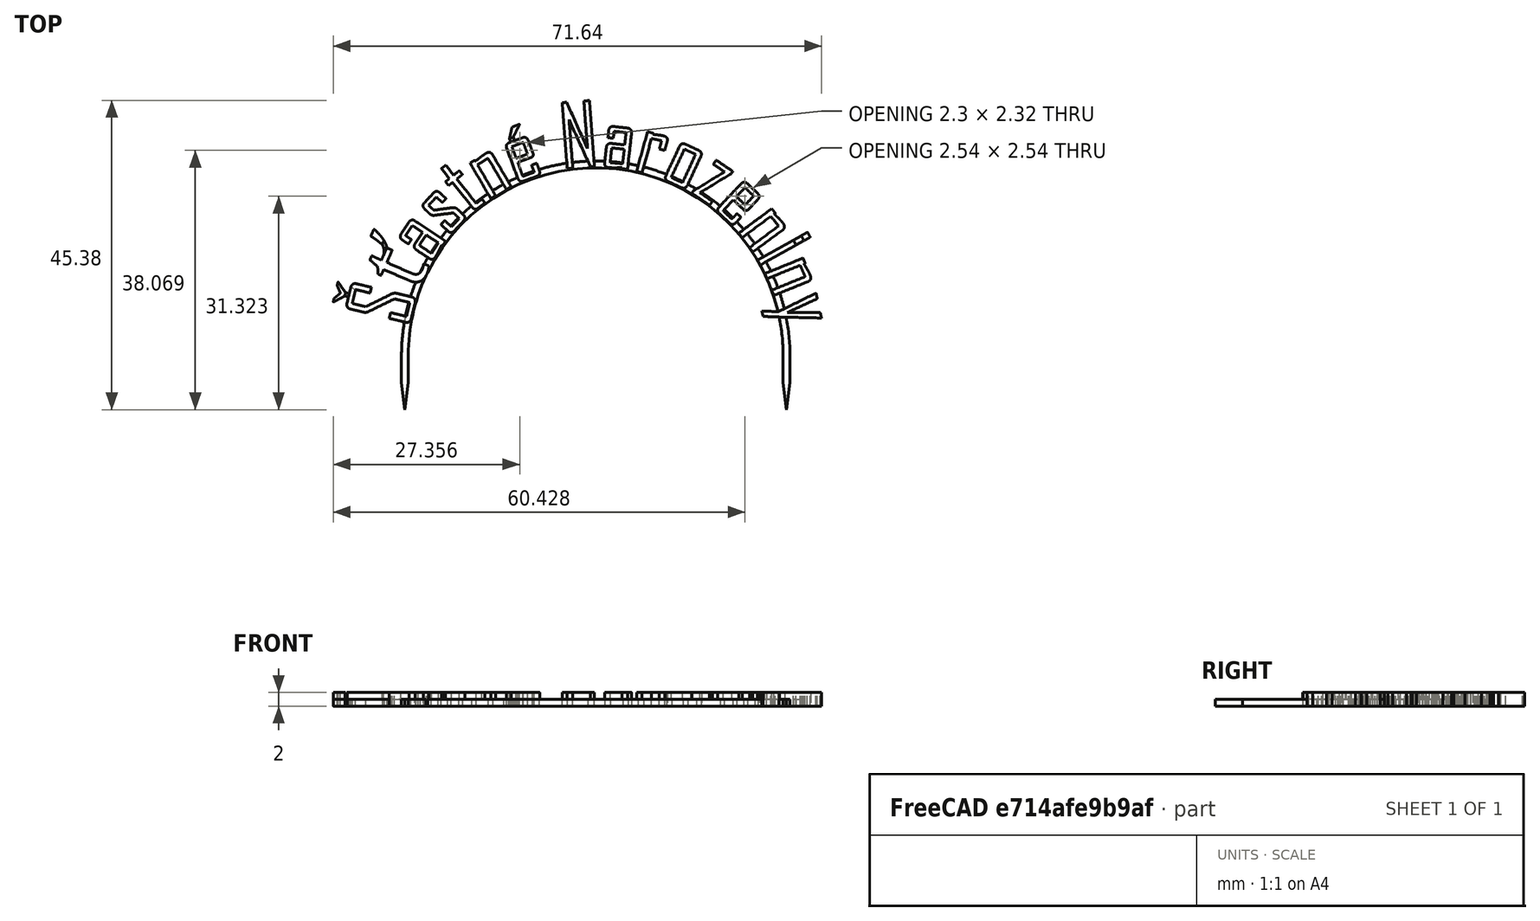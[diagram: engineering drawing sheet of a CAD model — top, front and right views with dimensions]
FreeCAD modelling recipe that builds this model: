
FCSTD DOCUMENT  (FreeCAD 0.20R29177 (Git))
Label: cake-topper-stastne-narozeniny
License: All rights reserved
LicenseURL: http://en.wikipedia.org/wiki/All_rights_reserved
objects: Part::Feature×31, Sketcher::SketchObject×11, PartDesign::Pad×10, App::DocumentObjectGroup×5, PartDesign::Body×2, App::TextDocument×1, Spreadsheet::Sheet×1, PartDesign::Plane×1, App::Part×1, Mesh::Feature×1
note: 65 computed .brp shape members not serialized (recipe doc carries the construction recipe); baked Part::Feature solids carry a one-line shape summary decoded from their .brp

FEATURE [App::TextDocument] Text_document  label="Text document"
FEATURE [Spreadsheet::Sheet] Spreadsheet
  cells = A1=Text height; B1=text_h; C1(dim_text_h)==2mm; A2=Text offset x; B2=text_x; C2(dim_text_x)==-105.3mm; A3=Text offset y; B3=text_y; C3(dim_text_y)==177.4mm; A4=Scaffold height; B4=scaffold_h; C4(dim_scaffold_h)==1mm; A5=Scaffold width; B5=scaffold_w; C5(dim_scaffold_w)==1mm; A6=Scaffold inner radius; B6=scaffold_ir; C6(dim_scaffold_ir)==27.5mm; A7=Scaffold outer radius; B7=scaffold_or; C7(dim_scaffold_or)==dim_scaffold_ir + dim_scaffold_w; A8=Tines length; B8=tine_l; C8(dim_tine_l)==4mm; A9=Tines shaft length; B9=tine_shaft_l; C9(dim_tine_shaft_l)==4mm
FEATURE [PartDesign::Plane] DatumPlane  label="BaseXYDatumPlane"
  Length = 72.6252
  MapMode = 5
  ResizeMode = 0
  Support = -> [XY_Plane]
  Width = 61.0934
FEATURE [Sketcher::SketchObject] Sketch001  label="ArcSketch"
  FullyConstrained = false
  MapMode = 5
  Support = -> [DatumPlane]
  expr: Constraints[15] = Spreadsheet.dim_scaffold_or
  expr: Constraints[37] = Spreadsheet.dim_tine_shaft_l
  expr: Constraints[38] = Spreadsheet.dim_tine_l
  expr: Constraints[59] = Spreadsheet.dim_scaffold_or
  expr: Constraints[6] = Spreadsheet.dim_scaffold_ir
  sketch-geometry (43):
    g0: ArcOfCircle CenterX=0 CenterY=0 CenterZ=0 NormalX=0 NormalY=0 NormalZ=1 AngleXU=0 Radius=27.5 StartAngle=0 EndAngle=3.14159
    g1: LineSegment StartX=-28.5 StartY=3.5e-15 StartZ=0 EndX=-27.5 EndY=3.4e-15 EndZ=0
    g2: LineSegment StartX=27.5 StartY=0 StartZ=0 EndX=28.5 EndY=0 EndZ=0
    g3: ArcOfCircle CenterX=0 CenterY=0 CenterZ=0 NormalX=0 NormalY=0 NormalZ=1 AngleXU=0 Radius=28.5 StartAngle=0 EndAngle=0.501542
    g4: ArcOfCircle CenterX=0 CenterY=0 CenterZ=0 NormalX=0 NormalY=0 NormalZ=1 AngleXU=0 Radius=28.5 StartAngle=0.501542 EndAngle=0.528912
    g5: LineSegment StartX=24.6057 StartY=14.3809 StartZ=0 EndX=31.0393 EndY=18.018 EndZ=0
    g6: LineSegment StartX=24.99 StartY=13.7022 StartZ=0 EndX=31.4232 EndY=17.339 EndZ=0
    g7: LineSegment StartX=31.0393 StartY=18.018 StartZ=0 EndX=31.4232 EndY=17.339 EndZ=0
    g8: LineSegment StartX=-28.5 StartY=3.5e-15 StartZ=0 EndX=-28.5 EndY=-4 EndZ=0
    g9: LineSegment StartX=-27.5 StartY=3.4e-15 StartZ=0 EndX=-27.5 EndY=-4 EndZ=0
    g10: LineSegment StartX=-28.5 StartY=-4 StartZ=0 EndX=-28 EndY=-8 EndZ=0
    g11: LineSegment StartX=-27.5 StartY=-4 StartZ=0 EndX=-28 EndY=-8 EndZ=0
    g12: LineSegment StartX=-28.5 StartY=-4 StartZ=0 EndX=-28 EndY=-4 EndZ=0
    g13: LineSegment StartX=-28 StartY=-4 StartZ=0 EndX=-27.5 EndY=-4 EndZ=0
    g14: LineSegment StartX=-28 StartY=-4 StartZ=0 EndX=-28 EndY=-8 EndZ=0
    g15: LineSegment StartX=27.5 StartY=-4 StartZ=0 EndX=28 EndY=-4 EndZ=0
    g16: LineSegment StartX=28 StartY=-4 StartZ=0 EndX=28.5 EndY=-4 EndZ=0
    g17: LineSegment StartX=28 StartY=-4 StartZ=0 EndX=28 EndY=-8 EndZ=0
    g18: LineSegment StartX=27.5 StartY=0 StartZ=0 EndX=27.5 EndY=-4 EndZ=0
    g19: LineSegment StartX=28.5 StartY=0 StartZ=0 EndX=28.5 EndY=-4 EndZ=0
    g20: LineSegment StartX=27.5 StartY=-4 StartZ=0 EndX=28 EndY=-8 EndZ=0
    g21: LineSegment StartX=28.5 StartY=-4 StartZ=0 EndX=28 EndY=-8 EndZ=0
    g22: LineSegment StartX=28.5 StartY=0 StartZ=0 EndX=28.5 EndY=28.5 EndZ=0
    g23: ArcOfCircle CenterX=0 CenterY=0 CenterZ=0 NormalX=0 NormalY=0 NormalZ=1 AngleXU=0 Radius=28.5 StartAngle=2.25167 EndAngle=2.29659
    g24: LineSegment StartX=-18.9162 StartY=21.3173 StartZ=0 EndX=-27.3759 EndY=31.2933 EndZ=0
    g25: LineSegment StartX=-17.94 StartY=22.1451 StartZ=0 EndX=-26.3997 EndY=32.1211 EndZ=0
    g26: LineSegment StartX=-27.3759 StartY=31.2933 StartZ=0 EndX=-26.3997 EndY=32.1211 EndZ=0
    g27: LineSegment StartX=-17.94 StartY=22.1451 StartZ=0 EndX=0 EndY=22.1451 EndZ=0
    g28: LineSegment StartX=28.5 StartY=28.5 StartZ=0 EndX=0 EndY=28.5 EndZ=0
    g29: LineSegment StartX=0 StartY=28.5 StartZ=0 EndX=-28.5 EndY=28.5 EndZ=0
    g30: LineSegment StartX=-28.5 StartY=3.5e-15 StartZ=0 EndX=-28.5 EndY=28.5 EndZ=0
    g31: ArcOfCircle CenterX=0 CenterY=0 CenterZ=0 NormalX=0 NormalY=0 NormalZ=1 AngleXU=0 Radius=28.5 StartAngle=1.87736 EndAngle=2.25167
    g32: ArcOfCircle CenterX=0 CenterY=0 CenterZ=0 NormalX=0 NormalY=0 NormalZ=1 AngleXU=0 Radius=28.5 StartAngle=0.528912 EndAngle=1.83244
    g33: ArcOfCircle CenterX=0 CenterY=0 CenterZ=0 NormalX=0 NormalY=0 NormalZ=1 AngleXU=0 Radius=28.5 StartAngle=1.83244 EndAngle=1.87736
    g34: LineSegment StartX=-8.60087 StartY=27.1712 StartZ=0 EndX=-12.2687 EndY=39.737 EndZ=0
    g35: LineSegment StartX=-7.37218 StartY=27.53 StartZ=0 EndX=-11.04 EndY=40.0956 EndZ=0
    g36: LineSegment StartX=-12.2687 StartY=39.737 StartZ=0 EndX=-11.04 EndY=40.0956 EndZ=0
    g37: LineSegment StartX=-11.04 StartY=40.0956 StartZ=0 EndX=0 EndY=40.0956 EndZ=0
    g38: LineSegment StartX=-7.37218 StartY=27.53 StartZ=0 EndX=-7.37218 EndY=28.5 EndZ=0
    g39: ArcOfCircle CenterX=0 CenterY=0 CenterZ=0 NormalX=0 NormalY=0 NormalZ=1 AngleXU=0 Radius=28.5 StartAngle=2.71804 EndAngle=3.14159
    g40: ArcOfCircle CenterX=0 CenterY=0 CenterZ=0 NormalX=0 NormalY=0 NormalZ=1 AngleXU=0 Radius=28.5 StartAngle=2.29659 EndAngle=2.67657
    g41: ArcOfCircle CenterX=0 CenterY=0 CenterZ=0 NormalX=0 NormalY=0 NormalZ=1 AngleXU=0 Radius=28.5 StartAngle=2.67657 EndAngle=2.71804
    g42: LineSegment StartX=24.99 StartY=13.7022 StartZ=0 EndX=28.5 EndY=13.7022 EndZ=0
  constraints (115):
    c: Coincident(g0,g-1)
    c: PointOnObject(g0,g-1)
    c: PointOnObject(g0,g-1)
    c: Coincident(g3,g0)
    c: PointOnObject(g39,g-1)
    c: PointOnObject(g3,g-1)
    c: Radius(g0) = 27.5
    c: Coincident(g1,g39)
    c: Coincident(g1,g0)
    c: Coincident(g2,g0)
    c: Coincident(g2,g3)
    c: Coincident(g4,g32)
    c: Coincident(g3,g32)
    c: Coincident(g3,g4)
    c: Coincident(g3,g4)
    c: Radius(g3) = 28.5
    c: Coincident(g5,g32)
    c: Coincident(g6,g3)
    c: Coincident(g7,g5)
    c: Parallel(g5,g6)
    c: Perpendicular(g7,g5)
    c: Coincident(g8,g39)
    c: Vertical(g8)
    c: Coincident(g9,g0)
    c: Vertical(g9)
    c: Coincident(g10,g8)
    c: Coincident(g11,g9)
    c: Coincident(g11,g10)
    c: Coincident(g12,g8)
    c: Horizontal(g12)
    c: Coincident(g13,g12)
    c: Coincident(g13,g9)
    c: Horizontal(g13)
    c: Coincident(g14,g12)
    c: Coincident(g14,g10)
    c: Equal(g13,g12)
    c: Vertical(g14)
    c: DistanceY(g9,g9) = 4
    c: DistanceY(g10,g9) = 4
    c: Horizontal(g15)
    c: Coincident(g16,g15)
    c: Horizontal(g16)
    c: Coincident(g17,g15)
    c: Vertical(g17)
    c: Coincident(g18,g0)
    c: Coincident(g18,g15)
    c: Vertical(g18)
    c: Coincident(g19,g3)
    c: Coincident(g19,g16)
    c: Vertical(g19)
    c: Coincident(g20,g18)
    c: Coincident(g20,g17)
    c: Coincident(g21,g19)
    c: Coincident(g21,g20)
    c: Equal(g18,g9)
    c: Equal(g17,g14)
    c: Equal(g16,g15)
    c: Coincident(g22,g3)
    c: Vertical(g22)
    c: DistanceY(g22,g22) = 28.5
    c: Coincident(g7,g6)
    c: Coincident(g23,g40)
    c: Coincident(g32,g40)
    c: Coincident(g31,g23)
    c: Coincident(g32,g23)
    c: Coincident(g24,g40)
    c: Coincident(g25,g31)
    c: Coincident(g26,g24)
    c: Coincident(g26,g25)
    c: Perpendicular(g24,g26)
    c: Perpendicular(g25,g26)
    c: Coincident(g27,g31)
    c: PointOnObject(g27,g-2)
    c: Horizontal(g27)
    c: Coincident(g28,g22)
    c: PointOnObject(g28,g-2)
    c: Horizontal(g28)
    c: Coincident(g29,g28)
    c: Horizontal(g29)
    c: Coincident(g30,g8)
    c: Coincident(g30,g29)
    c: Vertical(g30)
    c: DistanceX(g27,g27) = 17.94
    c: Distance(g26) = 1.28
    c: Distance(g25) = 13.08
    c: Coincident(g33,g31)
    c: Coincident(g32,g31)
    c: Coincident(g32,g33)
    c: Coincident(g32,g33)
    c: Coincident(g34,g31)
    c: Coincident(g35,g32)
    c: Coincident(g36,g34)
    c: Coincident(g36,g35)
    c: Perpendicular(g34,g36)
    c: Distance(g36) = 1.28
    c: Distance(g31,g32) = 1.28
    c: Distance(g35) = 13.09
    c: Coincident(g37,g35)
    c: PointOnObject(g37,g-2)
    c: Horizontal(g37)
    c: DistanceX(g37,g37) = 11.04
    c: Coincident(g38,g32)
    c: PointOnObject(g38,g29)
    c: Vertical(g38)
    c: DistanceY(g38,g38) = 0.97
    c: Coincident(g41,g39)
    c: Coincident(g40,g39)
    c: Coincident(g40,g41)
    c: Coincident(g40,g41)
    c: Coincident(g42,g3)
    c: PointOnObject(g42,g22)
    c: Horizontal(g42)
    c: Distance(g7) = 0.78
    c: Distance(g6) = 7.39
    c: DistanceX(g42,g42) = 3.51
FEATURE [PartDesign::Pad] Pad  label="ArcPad"
  Direction = (0,0,1)
  Length = 1
  Length2 = 10
  Profile = -> Sketch001
  ReferenceAxis = -> Sketch001 [N_Axis]
  Type = 0
  expr: Length = Spreadsheet.dim_scaffold_h
FEATURE [Part::Feature] path71269
  shape: bbox 10.09 x 5.737 x 2e-07 mm, 0 faces, 0 solids (baked)
FEATURE [Part::Feature] path71269001
  shape: bbox 1.822 x 2.922 x 2e-07 mm, 0 faces, 0 solids (baked)
FEATURE [Part::Feature] path71271
  shape: bbox 8.679 x 5.085 x 2e-07 mm, 0 faces, 0 solids (baked)
FEATURE [Part::Feature] path71271001
  shape: bbox 1.936 x 2.214 x 2e-07 mm, 0 faces, 0 solids (baked)
FEATURE [Part::Feature] path71273
  shape: bbox 6.743 x 5.932 x 2e-07 mm, 0 faces, 0 solids (baked)
FEATURE [Part::Feature] path71273001
  shape: bbox 2.796 x 2.735 x 2e-07 mm, 0 faces, 0 solids (baked)
FEATURE [Part::Feature] path71275
  shape: bbox 6.332 x 6.216 x 2e-07 mm, 0 faces, 0 solids (baked)
FEATURE [Part::Feature] path71277
  shape: bbox 6.399 x 6.535 x 2e-07 mm, 0 faces, 0 solids (baked)
FEATURE [Part::Feature] path71279
  shape: bbox 6.039 x 6.849 x 2e-07 mm, 0 faces, 0 solids (baked)
FEATURE [Part::Feature] path71281
  shape: bbox 5.094 x 6.662 x 2e-07 mm, 0 faces, 0 solids (baked)
FEATURE [Part::Feature] path71281001
  shape: bbox 2.296 x 2.321 x 2e-07 mm, 0 faces, 0 solids (baked)
FEATURE [Part::Feature] path71281002
  shape: bbox 1.478 x 2.097 x 2e-07 mm, 0 faces, 0 solids (baked)
FEATURE [Part::Feature] path71283
  shape: bbox 4.734 x 9.983 x 2e-07 mm, 0 faces, 0 solids (baked)
FEATURE [Part::Feature] path71285
  shape: bbox 4.088 x 6.368 x 2e-07 mm, 0 faces, 0 solids (baked)
FEATURE [Part::Feature] path71285001
  shape: bbox 2.069 x 2.323 x 2e-07 mm, 0 faces, 0 solids (baked)
FEATURE [Part::Feature] path71287
  shape: bbox 4.616 x 6.034 x 2e-07 mm, 0 faces, 0 solids (baked)
FEATURE [Part::Feature] path71289
  shape: bbox 5.465 x 6.708 x 2e-07 mm, 0 faces, 0 solids (baked)
FEATURE [Part::Feature] path71289001
  shape: bbox 3.583 x 4.921 x 2e-07 mm, 0 faces, 0 solids (baked)
FEATURE [Part::Feature] path71291
  shape: bbox 6.023 x 6.644 x 2e-07 mm, 0 faces, 0 solids (baked)
FEATURE [Part::Feature] path71293
  shape: bbox 6.291 x 6.392 x 2e-07 mm, 0 faces, 0 solids (baked)
FEATURE [Part::Feature] path71293001
  shape: bbox 2.537 x 2.539 x 2e-07 mm, 0 faces, 0 solids (baked)
FEATURE [Part::Feature] path71295
  shape: bbox 6.792 x 6.382 x 2e-07 mm, 0 faces, 0 solids (baked)
FEATURE [Part::Feature] path71297
  shape: bbox 1.318 x 1.24 x 2e-07 mm, 0 faces, 0 solids (baked)
FEATURE [Part::Feature] path71297001
  shape: bbox 5.658 x 3.663 x 2e-07 mm, 0 faces, 0 solids (baked)
FEATURE [Part::Feature] path71299
  shape: bbox 6.833 x 5.472 x 2e-07 mm, 0 faces, 0 solids (baked)
FEATURE [Part::Feature] path71301
  shape: bbox 8.742 x 3.659 x 2e-07 mm, 0 faces, 0 solids (baked)
FEATURE [App::DocumentObjectGroup] Group  label="StastneGroup"
  Group = -> [path71269,path71269001,path71273,path71273001,path71275,path71277,path71279,path71281,path71281001,path71281002]
FEATURE [App::DocumentObjectGroup] Group001  label="NarozeninyGroup"
  Group = -> [path71283,path71285,path71285001,path71287,path71289,path71289001,path71291,path71293,path71293001,path71295,path71297,path71297001,path71299,path71301]
FEATURE [Sketcher::SketchObject] Sketch  label="astneSketch"
  FullyConstrained = false
  Placement = pos=(-105.3,177.4,0) rot=(0,0,1;0rad)
  expr: .Placement.Base.x = Spreadsheet.dim_text_x
  expr: .Placement.Base.y = Spreadsheet.dim_text_y
  sketch-geometry (95):
    g0: BSplineCurve PolesCount=2 KnotsCount=2 Degree=1 IsPeriodic=0
    g1: BSplineCurve PolesCount=2 KnotsCount=2 Degree=1 IsPeriodic=0
    g2: BSplineCurve PolesCount=3 KnotsCount=2 Degree=2 IsPeriodic=0
    g3: BSplineCurve PolesCount=3 KnotsCount=2 Degree=2 IsPeriodic=0
    g4: BSplineCurve PolesCount=3 KnotsCount=2 Degree=2 IsPeriodic=0
    g5: BSplineCurve PolesCount=2 KnotsCount=2 Degree=1 IsPeriodic=0
    g6: BSplineCurve PolesCount=3 KnotsCount=2 Degree=2 IsPeriodic=0
    g7: BSplineCurve PolesCount=2 KnotsCount=2 Degree=1 IsPeriodic=0
    g8: BSplineCurve PolesCount=2 KnotsCount=2 Degree=1 IsPeriodic=0
    g9: BSplineCurve PolesCount=2 KnotsCount=2 Degree=1 IsPeriodic=0
    g10: BSplineCurve PolesCount=2 KnotsCount=2 Degree=1 IsPeriodic=0
    g11: BSplineCurve PolesCount=2 KnotsCount=2 Degree=1 IsPeriodic=0
    g12: BSplineCurve PolesCount=2 KnotsCount=2 Degree=1 IsPeriodic=0
    g13: BSplineCurve PolesCount=3 KnotsCount=2 Degree=2 IsPeriodic=0
    g14: BSplineCurve PolesCount=2 KnotsCount=2 Degree=1 IsPeriodic=0
    g15: BSplineCurve PolesCount=3 KnotsCount=2 Degree=2 IsPeriodic=0
    g16: BSplineCurve PolesCount=2 KnotsCount=2 Degree=1 IsPeriodic=0
    g17: BSplineCurve PolesCount=2 KnotsCount=2 Degree=1 IsPeriodic=0
    g18: BSplineCurve PolesCount=2 KnotsCount=2 Degree=1 IsPeriodic=0
    g19: BSplineCurve PolesCount=2 KnotsCount=2 Degree=1 IsPeriodic=0
    g20: BSplineCurve PolesCount=2 KnotsCount=2 Degree=1 IsPeriodic=0
    g21: BSplineCurve PolesCount=3 KnotsCount=2 Degree=2 IsPeriodic=0
    g22: BSplineCurve PolesCount=2 KnotsCount=2 Degree=1 IsPeriodic=0
    g23: BSplineCurve PolesCount=3 KnotsCount=2 Degree=2 IsPeriodic=0
    g24: BSplineCurve PolesCount=2 KnotsCount=2 Degree=1 IsPeriodic=0
    g25: BSplineCurve PolesCount=2 KnotsCount=2 Degree=1 IsPeriodic=0
    g26: BSplineCurve PolesCount=2 KnotsCount=2 Degree=1 IsPeriodic=0
    g27: BSplineCurve PolesCount=2 KnotsCount=2 Degree=1 IsPeriodic=0
    g28: BSplineCurve PolesCount=2 KnotsCount=2 Degree=1 IsPeriodic=0
    g29: BSplineCurve PolesCount=2 KnotsCount=2 Degree=1 IsPeriodic=0
    g30: BSplineCurve PolesCount=3 KnotsCount=2 Degree=2 IsPeriodic=0
    g31: BSplineCurve PolesCount=2 KnotsCount=2 Degree=1 IsPeriodic=0
    g32: BSplineCurve PolesCount=3 KnotsCount=2 Degree=2 IsPeriodic=0
    g33: BSplineCurve PolesCount=2 KnotsCount=2 Degree=1 IsPeriodic=0
    g34: BSplineCurve PolesCount=3 KnotsCount=2 Degree=2 IsPeriodic=0
    g35: BSplineCurve PolesCount=2 KnotsCount=2 Degree=1 IsPeriodic=0
    g36: BSplineCurve PolesCount=2 KnotsCount=2 Degree=1 IsPeriodic=0
    g37: BSplineCurve PolesCount=2 KnotsCount=2 Degree=1 IsPeriodic=0
    g38: BSplineCurve PolesCount=2 KnotsCount=2 Degree=1 IsPeriodic=0
    g39: BSplineCurve PolesCount=2 KnotsCount=2 Degree=1 IsPeriodic=0
    g40: BSplineCurve PolesCount=2 KnotsCount=2 Degree=1 IsPeriodic=0
    g41: BSplineCurve PolesCount=3 KnotsCount=2 Degree=2 IsPeriodic=0
    g42: BSplineCurve PolesCount=2 KnotsCount=2 Degree=1 IsPeriodic=0
    g43: BSplineCurve PolesCount=2 KnotsCount=2 Degree=1 IsPeriodic=0
    g44: BSplineCurve PolesCount=3 KnotsCount=2 Degree=2 IsPeriodic=0
    g45: BSplineCurve PolesCount=2 KnotsCount=2 Degree=1 IsPeriodic=0
    g46: BSplineCurve PolesCount=2 KnotsCount=2 Degree=1 IsPeriodic=0
    g47: BSplineCurve PolesCount=2 KnotsCount=2 Degree=1 IsPeriodic=0
    g48: BSplineCurve PolesCount=2 KnotsCount=2 Degree=1 IsPeriodic=0
    g49: BSplineCurve PolesCount=2 KnotsCount=2 Degree=1 IsPeriodic=0
    g50: BSplineCurve PolesCount=2 KnotsCount=2 Degree=1 IsPeriodic=0
    g51: BSplineCurve PolesCount=2 KnotsCount=2 Degree=1 IsPeriodic=0
    g52: BSplineCurve PolesCount=2 KnotsCount=2 Degree=1 IsPeriodic=0
    g53: BSplineCurve PolesCount=2 KnotsCount=2 Degree=1 IsPeriodic=0
    g54: BSplineCurve PolesCount=2 KnotsCount=2 Degree=1 IsPeriodic=0
    g55: BSplineCurve PolesCount=2 KnotsCount=2 Degree=1 IsPeriodic=0
    g56: BSplineCurve PolesCount=2 KnotsCount=2 Degree=1 IsPeriodic=0
    g57: BSplineCurve PolesCount=2 KnotsCount=2 Degree=1 IsPeriodic=0
    g58: BSplineCurve PolesCount=2 KnotsCount=2 Degree=1 IsPeriodic=0
    g59: BSplineCurve PolesCount=2 KnotsCount=2 Degree=1 IsPeriodic=0
    g60: BSplineCurve PolesCount=2 KnotsCount=2 Degree=1 IsPeriodic=0
    g61: BSplineCurve PolesCount=2 KnotsCount=2 Degree=1 IsPeriodic=0
    g62: BSplineCurve PolesCount=2 KnotsCount=2 Degree=1 IsPeriodic=0
    g63: BSplineCurve PolesCount=2 KnotsCount=2 Degree=1 IsPeriodic=0
    g64: BSplineCurve PolesCount=2 KnotsCount=2 Degree=1 IsPeriodic=0
    g65: BSplineCurve PolesCount=2 KnotsCount=2 Degree=1 IsPeriodic=0
    g66: BSplineCurve PolesCount=3 KnotsCount=2 Degree=2 IsPeriodic=0
    g67: BSplineCurve PolesCount=3 KnotsCount=2 Degree=2 IsPeriodic=0
    g68: BSplineCurve PolesCount=3 KnotsCount=2 Degree=2 IsPeriodic=0
    g69: BSplineCurve PolesCount=2 KnotsCount=2 Degree=1 IsPeriodic=0
    g70: BSplineCurve PolesCount=3 KnotsCount=2 Degree=2 IsPeriodic=0
    g71: BSplineCurve PolesCount=2 KnotsCount=2 Degree=1 IsPeriodic=0
    g72: BSplineCurve PolesCount=3 KnotsCount=2 Degree=2 IsPeriodic=0
    g73: BSplineCurve PolesCount=2 KnotsCount=2 Degree=1 IsPeriodic=0
    g74: BSplineCurve PolesCount=3 KnotsCount=2 Degree=2 IsPeriodic=0
    g75: BSplineCurve PolesCount=2 KnotsCount=2 Degree=1 IsPeriodic=0
    g76: BSplineCurve PolesCount=3 KnotsCount=2 Degree=2 IsPeriodic=0
    g77: BSplineCurve PolesCount=2 KnotsCount=2 Degree=1 IsPeriodic=0
    g78: BSplineCurve PolesCount=2 KnotsCount=2 Degree=1 IsPeriodic=0
    g79: BSplineCurve PolesCount=2 KnotsCount=2 Degree=1 IsPeriodic=0
    g80: BSplineCurve PolesCount=2 KnotsCount=2 Degree=1 IsPeriodic=0
    g81: BSplineCurve PolesCount=2 KnotsCount=2 Degree=1 IsPeriodic=0
    g82: BSplineCurve PolesCount=2 KnotsCount=2 Degree=1 IsPeriodic=0
    g83: BSplineCurve PolesCount=2 KnotsCount=2 Degree=1 IsPeriodic=0
    g84: BSplineCurve PolesCount=2 KnotsCount=2 Degree=1 IsPeriodic=0
    g85: BSplineCurve PolesCount=2 KnotsCount=2 Degree=1 IsPeriodic=0
    g86: BSplineCurve PolesCount=2 KnotsCount=2 Degree=1 IsPeriodic=0
    g87: BSplineCurve PolesCount=2 KnotsCount=2 Degree=1 IsPeriodic=0
    g88: BSplineCurve PolesCount=2 KnotsCount=2 Degree=1 IsPeriodic=0
    g89: BSplineCurve PolesCount=2 KnotsCount=2 Degree=1 IsPeriodic=0
    g90: BSplineCurve PolesCount=2 KnotsCount=2 Degree=1 IsPeriodic=0
    g91: BSplineCurve PolesCount=2 KnotsCount=2 Degree=1 IsPeriodic=0
    g92: BSplineCurve PolesCount=2 KnotsCount=2 Degree=1 IsPeriodic=0
    g93: BSplineCurve PolesCount=2 KnotsCount=2 Degree=1 IsPeriodic=0
    g94: BSplineCurve PolesCount=2 KnotsCount=2 Degree=1 IsPeriodic=0
  constraints (95):
    c: Coincident(g0,g1)
    c: Coincident(g1,g2)
    c: Coincident(g2,g3)
    c: Coincident(g3,g4)
    c: Coincident(g4,g5)
    c: Coincident(g5,g6)
    c: Coincident(g6,g7)
    c: Coincident(g7,g8)
    c: Coincident(g8,g9)
    c: Coincident(g9,g10)
    c: Coincident(g10,g11)
    c: Coincident(g11,g12)
    c: Coincident(g12,g13)
    c: Coincident(g13,g14)
    c: Coincident(g14,g15)
    c: Coincident(g15,g16)
    c: Coincident(g16,g0)
    c: Coincident(g17,g18)
    c: Coincident(g18,g19)
    c: Coincident(g19,g20)
    c: Coincident(g20,g17)
    c: Coincident(g21,g22)
    c: Coincident(g22,g23)
    c: Coincident(g23,g24)
    c: Coincident(g24,g25)
    c: Coincident(g25,g26)
    c: Coincident(g26,g27)
    c: Coincident(g27,g28)
    c: Coincident(g28,g29)
    c: Coincident(g29,g30)
    c: Coincident(g30,g31)
    c: Coincident(g31,g32)
    c: Coincident(g32,g33)
    c: Coincident(g33,g34)
    c: Coincident(g34,g35)
    c: Coincident(g35,g36)
    c: Coincident(g36,g37)
    c: Coincident(g37,g38)
    c: Coincident(g38,g39)
    c: Coincident(g39,g40)
    c: Coincident(g40,g41)
    c: Coincident(g41,g42)
    c: Coincident(g42,g21)
    c: Coincident(g43,g44)
    c: Coincident(g44,g45)
    c: Coincident(g45,g46)
    c: Coincident(g46,g47)
    c: Coincident(g47,g48)
    c: Coincident(g48,g49)
    c: Coincident(g49,g50)
    c: Coincident(g50,g51)
    c: Coincident(g51,g52)
    c: Coincident(g52,g53)
    c: Coincident(g53,g54)
    c: Coincident(g54,g55)
    c: Coincident(g55,g56)
    c: Coincident(g56,g57)
    c: Coincident(g57,g43)
    c: Coincident(g58,g59)
    c: Coincident(g59,g60)
    c: Coincident(g60,g61)
    c: Coincident(g61,g62)
    c: Coincident(g62,g63)
    c: Coincident(g63,g64)
    c: Coincident(g64,g65)
    c: Coincident(g65,g66)
    c: Coincident(g66,g67)
    c: Coincident(g67,g68)
    c: Coincident(g68,g69)
    c: Coincident(g69,g58)
    c: Coincident(g70,g71)
    c: Coincident(g71,g72)
    c: Coincident(g72,g73)
    c: Coincident(g73,g74)
    c: Coincident(g74,g75)
    c: Coincident(g75,g76)
    c: Coincident(g76,g77)
    c: Coincident(g77,g78)
    c: Coincident(g78,g79)
    c: Coincident(g79,g80)
    c: Coincident(g80,g81)
    c: Coincident(g81,g82)
    c: Coincident(g82,g83)
    c: Coincident(g83,g84)
    c: Coincident(g84,g70)
    c: Coincident(g85,g86)
    c: Coincident(g86,g87)
    c: Coincident(g87,g88)
    c: Coincident(g88,g85)
    c: Coincident(g89,g90)
    c: Coincident(g90,g91)
    c: Coincident(g91,g92)
    c: Coincident(g92,g93)
    c: Coincident(g93,g94)
    c: Coincident(g94,g89)
FEATURE [Sketcher::SketchObject] Sketch002  label="NarozeninySketch"
  FullyConstrained = false
  Placement = pos=(-105.3,177.4,0) rot=(0,0,1;0rad)
  expr: .Placement.Base.x = Spreadsheet.dim_text_x
  expr: .Placement.Base.y = Spreadsheet.dim_text_y
  sketch-geometry (125):
    g0: BSplineCurve PolesCount=2 KnotsCount=2 Degree=1 IsPeriodic=0
    g1: BSplineCurve PolesCount=2 KnotsCount=2 Degree=1 IsPeriodic=0
    g2: BSplineCurve PolesCount=2 KnotsCount=2 Degree=1 IsPeriodic=0
    g3: BSplineCurve PolesCount=2 KnotsCount=2 Degree=1 IsPeriodic=0
    g4: BSplineCurve PolesCount=2 KnotsCount=2 Degree=1 IsPeriodic=0
    g5: BSplineCurve PolesCount=2 KnotsCount=2 Degree=1 IsPeriodic=0
    g6: BSplineCurve PolesCount=2 KnotsCount=2 Degree=1 IsPeriodic=0
    g7: BSplineCurve PolesCount=2 KnotsCount=2 Degree=1 IsPeriodic=0
    g8: BSplineCurve PolesCount=2 KnotsCount=2 Degree=1 IsPeriodic=0
    g9: BSplineCurve PolesCount=2 KnotsCount=2 Degree=1 IsPeriodic=0
    g10: BSplineCurve PolesCount=2 KnotsCount=2 Degree=1 IsPeriodic=0
    g11: BSplineCurve PolesCount=2 KnotsCount=2 Degree=1 IsPeriodic=0
    g12: BSplineCurve PolesCount=3 KnotsCount=2 Degree=2 IsPeriodic=0
    g13: BSplineCurve PolesCount=3 KnotsCount=2 Degree=2 IsPeriodic=0
    g14: BSplineCurve PolesCount=3 KnotsCount=2 Degree=2 IsPeriodic=0
    g15: BSplineCurve PolesCount=2 KnotsCount=2 Degree=1 IsPeriodic=0
    g16: BSplineCurve PolesCount=3 KnotsCount=2 Degree=2 IsPeriodic=0
    g17: BSplineCurve PolesCount=2 KnotsCount=2 Degree=1 IsPeriodic=0
    g18: BSplineCurve PolesCount=2 KnotsCount=2 Degree=1 IsPeriodic=0
    g19: BSplineCurve PolesCount=2 KnotsCount=2 Degree=1 IsPeriodic=0
    g20: BSplineCurve PolesCount=2 KnotsCount=2 Degree=1 IsPeriodic=0
    g21: BSplineCurve PolesCount=2 KnotsCount=2 Degree=1 IsPeriodic=0
    g22: BSplineCurve PolesCount=2 KnotsCount=2 Degree=1 IsPeriodic=0
    g23: BSplineCurve PolesCount=3 KnotsCount=2 Degree=2 IsPeriodic=0
    g24: BSplineCurve PolesCount=2 KnotsCount=2 Degree=1 IsPeriodic=0
    g25: BSplineCurve PolesCount=3 KnotsCount=2 Degree=2 IsPeriodic=0
    g26: BSplineCurve PolesCount=2 KnotsCount=2 Degree=1 IsPeriodic=0
    g27: BSplineCurve PolesCount=2 KnotsCount=2 Degree=1 IsPeriodic=0
    g28: BSplineCurve PolesCount=2 KnotsCount=2 Degree=1 IsPeriodic=0
    g29: BSplineCurve PolesCount=2 KnotsCount=2 Degree=1 IsPeriodic=0
    g30: BSplineCurve PolesCount=2 KnotsCount=2 Degree=1 IsPeriodic=0
    g31: BSplineCurve PolesCount=2 KnotsCount=2 Degree=1 IsPeriodic=0
    g32: BSplineCurve PolesCount=2 KnotsCount=2 Degree=1 IsPeriodic=0
    g33: BSplineCurve PolesCount=2 KnotsCount=2 Degree=1 IsPeriodic=0
    g34: BSplineCurve PolesCount=2 KnotsCount=2 Degree=1 IsPeriodic=0
    g35: BSplineCurve PolesCount=2 KnotsCount=2 Degree=1 IsPeriodic=0
    g36: BSplineCurve PolesCount=2 KnotsCount=2 Degree=1 IsPeriodic=0
    g37: BSplineCurve PolesCount=2 KnotsCount=2 Degree=1 IsPeriodic=0
    g38: BSplineCurve PolesCount=2 KnotsCount=2 Degree=1 IsPeriodic=0
    g39: BSplineCurve PolesCount=3 KnotsCount=2 Degree=2 IsPeriodic=0
    g40: BSplineCurve PolesCount=3 KnotsCount=2 Degree=2 IsPeriodic=0
    g41: BSplineCurve PolesCount=3 KnotsCount=2 Degree=2 IsPeriodic=0
    g42: BSplineCurve PolesCount=2 KnotsCount=2 Degree=1 IsPeriodic=0
    g43: BSplineCurve PolesCount=3 KnotsCount=2 Degree=2 IsPeriodic=0
    g44: BSplineCurve PolesCount=2 KnotsCount=2 Degree=1 IsPeriodic=0
    g45: BSplineCurve PolesCount=3 KnotsCount=2 Degree=2 IsPeriodic=0
    g46: BSplineCurve PolesCount=2 KnotsCount=2 Degree=1 IsPeriodic=0
    g47: BSplineCurve PolesCount=3 KnotsCount=2 Degree=2 IsPeriodic=0
    g48: BSplineCurve PolesCount=2 KnotsCount=2 Degree=1 IsPeriodic=0
    g49: BSplineCurve PolesCount=3 KnotsCount=2 Degree=2 IsPeriodic=0
    g50: BSplineCurve PolesCount=2 KnotsCount=2 Degree=1 IsPeriodic=0
    g51: BSplineCurve PolesCount=2 KnotsCount=2 Degree=1 IsPeriodic=0
    g52: BSplineCurve PolesCount=2 KnotsCount=2 Degree=1 IsPeriodic=0
    g53: BSplineCurve PolesCount=2 KnotsCount=2 Degree=1 IsPeriodic=0
    g54: BSplineCurve PolesCount=2 KnotsCount=2 Degree=1 IsPeriodic=0
    g55: BSplineCurve PolesCount=2 KnotsCount=2 Degree=1 IsPeriodic=0
    g56: BSplineCurve PolesCount=2 KnotsCount=2 Degree=1 IsPeriodic=0
    g57: BSplineCurve PolesCount=2 KnotsCount=2 Degree=1 IsPeriodic=0
    g58: BSplineCurve PolesCount=2 KnotsCount=2 Degree=1 IsPeriodic=0
    g59: BSplineCurve PolesCount=2 KnotsCount=2 Degree=1 IsPeriodic=0
    g60: BSplineCurve PolesCount=2 KnotsCount=2 Degree=1 IsPeriodic=0
    g61: BSplineCurve PolesCount=2 KnotsCount=2 Degree=1 IsPeriodic=0
    g62: BSplineCurve PolesCount=2 KnotsCount=2 Degree=1 IsPeriodic=0
    g63: BSplineCurve PolesCount=2 KnotsCount=2 Degree=1 IsPeriodic=0
    g64: BSplineCurve PolesCount=2 KnotsCount=2 Degree=1 IsPeriodic=0
    g65: BSplineCurve PolesCount=3 KnotsCount=2 Degree=2 IsPeriodic=0
    g66: BSplineCurve PolesCount=2 KnotsCount=2 Degree=1 IsPeriodic=0
    g67: BSplineCurve PolesCount=3 KnotsCount=2 Degree=2 IsPeriodic=0
    g68: BSplineCurve PolesCount=2 KnotsCount=2 Degree=1 IsPeriodic=0
    g69: BSplineCurve PolesCount=3 KnotsCount=2 Degree=2 IsPeriodic=0
    g70: BSplineCurve PolesCount=2 KnotsCount=2 Degree=1 IsPeriodic=0
    g71: BSplineCurve PolesCount=3 KnotsCount=2 Degree=2 IsPeriodic=0
    g72: BSplineCurve PolesCount=2 KnotsCount=2 Degree=1 IsPeriodic=0
    g73: BSplineCurve PolesCount=2 KnotsCount=2 Degree=1 IsPeriodic=0
    g74: BSplineCurve PolesCount=2 KnotsCount=2 Degree=1 IsPeriodic=0
    g75: BSplineCurve PolesCount=2 KnotsCount=2 Degree=1 IsPeriodic=0
    g76: BSplineCurve PolesCount=2 KnotsCount=2 Degree=1 IsPeriodic=0
    g77: BSplineCurve PolesCount=2 KnotsCount=2 Degree=1 IsPeriodic=0
    g78: BSplineCurve PolesCount=2 KnotsCount=2 Degree=1 IsPeriodic=0
    g79: BSplineCurve PolesCount=2 KnotsCount=2 Degree=1 IsPeriodic=0
    g80: BSplineCurve PolesCount=2 KnotsCount=2 Degree=1 IsPeriodic=0
    g81: BSplineCurve PolesCount=2 KnotsCount=2 Degree=1 IsPeriodic=0
    g82: BSplineCurve PolesCount=2 KnotsCount=2 Degree=1 IsPeriodic=0
    g83: BSplineCurve PolesCount=2 KnotsCount=2 Degree=1 IsPeriodic=0
    g84: BSplineCurve PolesCount=2 KnotsCount=2 Degree=1 IsPeriodic=0
    g85: BSplineCurve PolesCount=2 KnotsCount=2 Degree=1 IsPeriodic=0
    g86: BSplineCurve PolesCount=2 KnotsCount=2 Degree=1 IsPeriodic=0
    g87: BSplineCurve PolesCount=2 KnotsCount=2 Degree=1 IsPeriodic=0
    g88: BSplineCurve PolesCount=2 KnotsCount=2 Degree=1 IsPeriodic=0
    g89: BSplineCurve PolesCount=2 KnotsCount=2 Degree=1 IsPeriodic=0
    g90: BSplineCurve PolesCount=2 KnotsCount=2 Degree=1 IsPeriodic=0
    g91: BSplineCurve PolesCount=2 KnotsCount=2 Degree=1 IsPeriodic=0
    g92: BSplineCurve PolesCount=3 KnotsCount=2 Degree=2 IsPeriodic=0
    g93: BSplineCurve PolesCount=3 KnotsCount=2 Degree=2 IsPeriodic=0
    g94: BSplineCurve PolesCount=3 KnotsCount=2 Degree=2 IsPeriodic=0
    g95: BSplineCurve PolesCount=2 KnotsCount=2 Degree=1 IsPeriodic=0
    g96: BSplineCurve PolesCount=2 KnotsCount=2 Degree=1 IsPeriodic=0
    g97: BSplineCurve PolesCount=2 KnotsCount=2 Degree=1 IsPeriodic=0
    g98: BSplineCurve PolesCount=2 KnotsCount=2 Degree=1 IsPeriodic=0
    g99: BSplineCurve PolesCount=2 KnotsCount=2 Degree=1 IsPeriodic=0
    g100: BSplineCurve PolesCount=2 KnotsCount=2 Degree=1 IsPeriodic=0
    g101: BSplineCurve PolesCount=2 KnotsCount=2 Degree=1 IsPeriodic=0
    g102: BSplineCurve PolesCount=2 KnotsCount=2 Degree=1 IsPeriodic=0
    g103: BSplineCurve PolesCount=2 KnotsCount=2 Degree=1 IsPeriodic=0
    g104: BSplineCurve PolesCount=2 KnotsCount=2 Degree=1 IsPeriodic=0
    g105: BSplineCurve PolesCount=2 KnotsCount=2 Degree=1 IsPeriodic=0
    g106: BSplineCurve PolesCount=2 KnotsCount=2 Degree=1 IsPeriodic=0
    g107: BSplineCurve PolesCount=2 KnotsCount=2 Degree=1 IsPeriodic=0
    g108: BSplineCurve PolesCount=2 KnotsCount=2 Degree=1 IsPeriodic=0
    g109: BSplineCurve PolesCount=2 KnotsCount=2 Degree=1 IsPeriodic=0
    g110: BSplineCurve PolesCount=2 KnotsCount=2 Degree=1 IsPeriodic=0
    g111: BSplineCurve PolesCount=2 KnotsCount=2 Degree=1 IsPeriodic=0
    g112: BSplineCurve PolesCount=3 KnotsCount=2 Degree=2 IsPeriodic=0
    g113: BSplineCurve PolesCount=3 KnotsCount=2 Degree=2 IsPeriodic=0
    g114: BSplineCurve PolesCount=3 KnotsCount=2 Degree=2 IsPeriodic=0
    g115: BSplineCurve PolesCount=2 KnotsCount=2 Degree=1 IsPeriodic=0
    g116: BSplineCurve PolesCount=2 KnotsCount=2 Degree=1 IsPeriodic=0
    g117: BSplineCurve PolesCount=2 KnotsCount=2 Degree=1 IsPeriodic=0
    g118: BSplineCurve PolesCount=2 KnotsCount=2 Degree=1 IsPeriodic=0
    g119: BSplineCurve PolesCount=2 KnotsCount=2 Degree=1 IsPeriodic=0
    g120: BSplineCurve PolesCount=2 KnotsCount=2 Degree=1 IsPeriodic=0
    g121: BSplineCurve PolesCount=2 KnotsCount=2 Degree=1 IsPeriodic=0
    g122: BSplineCurve PolesCount=2 KnotsCount=2 Degree=1 IsPeriodic=0
    g123: BSplineCurve PolesCount=2 KnotsCount=2 Degree=1 IsPeriodic=0
    g124: BSplineCurve PolesCount=2 KnotsCount=2 Degree=1 IsPeriodic=0
  constraints (125):
    c: Coincident(g0,g1)
    c: Coincident(g1,g2)
    c: Coincident(g2,g3)
    c: Coincident(g3,g4)
    c: Coincident(g4,g5)
    c: Coincident(g5,g6)
    c: Coincident(g6,g7)
    c: Coincident(g7,g8)
    c: Coincident(g8,g9)
    c: Coincident(g9,g0)
    c: Coincident(g10,g11)
    c: Coincident(g11,g12)
    c: Coincident(g12,g13)
    c: Coincident(g13,g14)
    c: Coincident(g14,g15)
    c: Coincident(g15,g16)
    c: Coincident(g16,g17)
    c: Coincident(g17,g18)
    c: Coincident(g18,g19)
    c: Coincident(g19,g20)
    c: Coincident(g20,g21)
    c: Coincident(g21,g22)
    c: Coincident(g22,g23)
    c: Coincident(g23,g24)
    c: Coincident(g24,g25)
    c: Coincident(g25,g26)
    c: Coincident(g26,g10)
    c: Coincident(g27,g28)
    c: Coincident(g28,g29)
    c: Coincident(g29,g30)
    c: Coincident(g30,g27)
    c: Coincident(g31,g32)
    c: Coincident(g32,g33)
    c: Coincident(g33,g34)
    c: Coincident(g34,g35)
    c: Coincident(g35,g36)
    c: Coincident(g36,g37)
    c: Coincident(g37,g38)
    c: Coincident(g38,g39)
    c: Coincident(g39,g40)
    c: Coincident(g40,g41)
    c: Coincident(g41,g42)
    c: Coincident(g42,g31)
    c: Coincident(g43,g44)
    c: Coincident(g44,g45)
    c: Coincident(g45,g46)
    c: Coincident(g46,g47)
    c: Coincident(g47,g48)
    c: Coincident(g48,g49)
    c: Coincident(g49,g50)
    c: Coincident(g50,g43)
    c: Coincident(g51,g52)
    c: Coincident(g52,g53)
    c: Coincident(g53,g54)
    c: Coincident(g54,g51)
    c: Coincident(g55,g56)
    c: Coincident(g56,g57)
    c: Coincident(g57,g58)
    c: Coincident(g58,g59)
    c: Coincident(g59,g60)
    c: Coincident(g60,g61)
    c: Coincident(g61,g62)
    c: Coincident(g62,g63)
    c: Coincident(g63,g64)
    c: Coincident(g64,g55)
    c: Coincident(g65,g66)
    c: Coincident(g66,g67)
    c: Coincident(g67,g68)
    c: Coincident(g68,g69)
    c: Coincident(g69,g70)
    c: Coincident(g70,g71)
    c: Coincident(g71,g72)
    c: Coincident(g72,g73)
    c: Coincident(g73,g74)
    c: Coincident(g74,g75)
    c: Coincident(g75,g76)
    c: Coincident(g76,g77)
    c: Coincident(g77,g78)
    c: Coincident(g78,g79)
    c: Coincident(g79,g65)
    c: Coincident(g80,g81)
    c: Coincident(g81,g82)
    c: Coincident(g82,g83)
    c: Coincident(g83,g80)
    c: Coincident(g84,g85)
    c: Coincident(g85,g86)
    c: Coincident(g86,g87)
    c: Coincident(g87,g88)
    c: Coincident(g88,g89)
    c: Coincident(g89,g90)
    c: Coincident(g90,g91)
    c: Coincident(g91,g92)
    c: Coincident(g92,g93)
    c: Coincident(g93,g94)
    c: Coincident(g94,g95)
    c: Coincident(g95,g84)
    c: Coincident(g96,g97)
    c: Coincident(g97,g98)
    c: Coincident(g98,g99)
    c: Coincident(g99,g96)
    c: Coincident(g100,g101)
    c: Coincident(g101,g102)
    c: Coincident(g102,g103)
    c: Coincident(g103,g100)
    c: Coincident(g104,g105)
    c: Coincident(g105,g106)
    c: Coincident(g106,g107)
    c: Coincident(g107,g108)
    c: Coincident(g108,g109)
    c: Coincident(g109,g110)
    c: Coincident(g110,g111)
    c: Coincident(g111,g112)
    c: Coincident(g112,g113)
    c: Coincident(g113,g114)
    c: Coincident(g114,g115)
    c: Coincident(g115,g104)
    c: Coincident(g116,g117)
    c: Coincident(g117,g118)
    c: Coincident(g118,g119)
    c: Coincident(g119,g120)
    c: Coincident(g120,g121)
    c: Coincident(g121,g122)
    c: Coincident(g122,g123)
    c: Coincident(g123,g124)
    c: Coincident(g124,g116)
FEATURE [App::DocumentObjectGroup] Group003  label="TGroup"
  Group = -> [path71271,path71271001]
FEATURE [Part::Feature] path71297002
  shape: bbox 1.822 x 2.922 x 2e-07 mm, 0 faces, 0 solids (baked)
FEATURE [Part::Feature] path71297003
  shape: bbox 10.09 x 5.737 x 2e-07 mm, 0 faces, 0 solids (baked)
FEATURE [App::DocumentObjectGroup] Group002  label="SGroup"
  Group = -> [path71297002,path71297003]
FEATURE [Part::Feature] path71297008
  shape: bbox 5.094 x 6.662 x 2e-07 mm, 0 faces, 0 solids (baked)
FEATURE [Part::Feature] path71297009
  shape: bbox 2.296 x 2.321 x 2e-07 mm, 0 faces, 0 solids (baked)
FEATURE [Part::Feature] path71297010
  shape: bbox 1.478 x 2.097 x 2e-07 mm, 0 faces, 0 solids (baked)
FEATURE [App::DocumentObjectGroup] Group004  label="EGroup"
  Group = -> [path71297008,path71297009,path71297010]
FEATURE [Sketcher::SketchObject] Sketch003  label="TScaffoldSketch"
  FullyConstrained = false
  Placement = pos=(-105.3,177.4,0) rot=(0,0,1;0rad)
  expr: .Placement.Base.x = Spreadsheet.dim_text_x
  expr: .Placement.Base.y = Spreadsheet.dim_text_y
  sketch-geometry (37):
    g0: BSplineCurve PolesCount=3 KnotsCount=2 Degree=2 IsPeriodic=0
    g1: BSplineCurve PolesCount=3 KnotsCount=2 Degree=2 IsPeriodic=0
    g2: BSplineCurve PolesCount=2 KnotsCount=2 Degree=1 IsPeriodic=0
    g3: BSplineCurve PolesCount=3 KnotsCount=2 Degree=2 IsPeriodic=0
    g4: BSplineCurve PolesCount=3 KnotsCount=2 Degree=2 IsPeriodic=0
    g5: BSplineCurve PolesCount=3 KnotsCount=2 Degree=2 IsPeriodic=0
    g6: BSplineCurve PolesCount=3 KnotsCount=2 Degree=2 IsPeriodic=0
    g7: BSplineCurve PolesCount=3 KnotsCount=2 Degree=2 IsPeriodic=0
    g8: BSplineCurve PolesCount=2 KnotsCount=2 Degree=1 IsPeriodic=0
    g9: BSplineCurve PolesCount=2 KnotsCount=2 Degree=1 IsPeriodic=0
    g10: BSplineCurve PolesCount=2 KnotsCount=2 Degree=1 IsPeriodic=0
    g11: BSplineCurve PolesCount=2 KnotsCount=2 Degree=1 IsPeriodic=0
    g12: BSplineCurve PolesCount=2 KnotsCount=2 Degree=1 IsPeriodic=0
    g13: BSplineCurve PolesCount=2 KnotsCount=2 Degree=1 IsPeriodic=0
    g14: BSplineCurve PolesCount=2 KnotsCount=2 Degree=1 IsPeriodic=0
    g15: BSplineCurve PolesCount=2 KnotsCount=2 Degree=1 IsPeriodic=0
    g16: BSplineCurve PolesCount=2 KnotsCount=2 Degree=1 IsPeriodic=0
    g17: BSplineCurve PolesCount=2 KnotsCount=2 Degree=1 IsPeriodic=0
    g18: BSplineCurve PolesCount=2 KnotsCount=2 Degree=1 IsPeriodic=0
    g19: BSplineCurve PolesCount=3 KnotsCount=2 Degree=2 IsPeriodic=0
    g20: BSplineCurve PolesCount=3 KnotsCount=2 Degree=2 IsPeriodic=0
    g21: BSplineCurve PolesCount=2 KnotsCount=2 Degree=1 IsPeriodic=0
    g22: BSplineCurve PolesCount=3 KnotsCount=2 Degree=2 IsPeriodic=0
    g23: BSplineCurve PolesCount=3 KnotsCount=2 Degree=2 IsPeriodic=0
    g24: BSplineCurve PolesCount=3 KnotsCount=2 Degree=2 IsPeriodic=0
    g25: BSplineCurve PolesCount=2 KnotsCount=2 Degree=1 IsPeriodic=0
    g26: BSplineCurve PolesCount=2 KnotsCount=2 Degree=1 IsPeriodic=0
    g27: BSplineCurve PolesCount=3 KnotsCount=2 Degree=2 IsPeriodic=0
    g28: BSplineCurve PolesCount=3 KnotsCount=2 Degree=2 IsPeriodic=0
    g29: BSplineCurve PolesCount=3 KnotsCount=2 Degree=2 IsPeriodic=0
    g30: BSplineCurve PolesCount=2 KnotsCount=2 Degree=1 IsPeriodic=0
    g31: ArcOfCircle CenterX=72.1817 CenterY=-162.007 CenterZ=0 NormalX=0 NormalY=0 NormalZ=1 AngleXU=0 Radius=2.48576 StartAngle=6.20549 EndAngle=6.89961
    g32: ArcOfCircle CenterX=72.2151 CenterY=-162.17 CenterZ=0 NormalX=0 NormalY=0 NormalZ=1 AngleXU=0 Radius=2.04155 StartAngle=5.94352 EndAngle=6.82901
    g33: LineSegment StartX=73.96 StartY=-161.11 StartZ=0 EndX=74.21 EndY=-160.57 EndZ=0
    g34: LineSegment StartX=74.14 StartY=-162.85 StartZ=0 EndX=74.66 EndY=-162.2 EndZ=0
    g35: LineSegment StartX=74.6459 StartY=-163.784 StartZ=0 EndX=74.66 EndY=-162.2 EndZ=0
    g36: LineSegment StartX=74.1953 StartY=-164.807 StartZ=0 EndX=74.14 EndY=-162.85 EndZ=0
  constraints (47):
    c: Coincident(g0,g1)
    c: Coincident(g1,g2)
    c: Coincident(g2,g3)
    c: Coincident(g3,g4)
    c: Coincident(g4,g5)
    c: Coincident(g5,g6)
    c: Coincident(g6,g7)
    c: Coincident(g7,g8)
    c: Coincident(g8,g9)
    c: Coincident(g9,g10)
    c: Coincident(g10,g11)
    c: Coincident(g11,g12)
    c: Coincident(g12,g13)
    c: Coincident(g13,g14)
    c: Coincident(g14,g15)
    c: Coincident(g15,g16)
    c: Coincident(g16,g17)
    c: Coincident(g17,g18)
    c: Coincident(g18,g19)
    c: Coincident(g19,g20)
    c: Coincident(g20,g0)
    c: Coincident(g21,g22)
    c: Coincident(g22,g23)
    c: Coincident(g23,g24)
    c: Coincident(g24,g25)
    c: Coincident(g25,g26)
    c: Coincident(g26,g27)
    c: Coincident(g27,g28)
    c: Coincident(g28,g29)
    c: Coincident(g29,g30)
    c: Coincident(g30,g21)
    c: Coincident(g34,g32)
    c: Coincident(g31,g34)
    c: Coincident(g33,g31)
    c: Coincident(g33,g32)
    c: DistanceX(g32) = 73.96
    c: DistanceY(g32) = -161.11
    c: DistanceX(g31) = 74.21
    c: DistanceY(g31) = -160.57
    c: DistanceX(g32) = 74.14
    c: DistanceY(g32) = -162.85
    c: DistanceY(g31) = -162.2
    c: DistanceX(g31) = 74.66
    c: Coincident(g35,g18)
    c: Coincident(g31,g35)
    c: Coincident(g36,g8)
    c: Coincident(g36,g32)
FEATURE [Sketcher::SketchObject] Sketch004  label="SScaffoldSketch"
  FullyConstrained = false
  Placement = pos=(-105.3,177.4,0) rot=(0,0,1;0rad)
  expr: .Placement.Base.x = Spreadsheet.dim_text_x
  expr: .Placement.Base.y = Spreadsheet.dim_text_y
  sketch-geometry (41):
    g0: BSplineCurve PolesCount=2 KnotsCount=2 Degree=1 IsPeriodic=0
    g1: BSplineCurve PolesCount=2 KnotsCount=2 Degree=1 IsPeriodic=0
    g2: BSplineCurve PolesCount=2 KnotsCount=2 Degree=1 IsPeriodic=0
    g3: BSplineCurve PolesCount=2 KnotsCount=2 Degree=1 IsPeriodic=0
    g4: BSplineCurve PolesCount=2 KnotsCount=2 Degree=1 IsPeriodic=0
    g5: BSplineCurve PolesCount=2 KnotsCount=2 Degree=1 IsPeriodic=0
    g6: BSplineCurve PolesCount=2 KnotsCount=2 Degree=1 IsPeriodic=0
    g7: BSplineCurve PolesCount=2 KnotsCount=2 Degree=1 IsPeriodic=0
    g8: BSplineCurve PolesCount=2 KnotsCount=2 Degree=1 IsPeriodic=0
    g9: BSplineCurve PolesCount=3 KnotsCount=2 Degree=2 IsPeriodic=0
    g10: BSplineCurve PolesCount=3 KnotsCount=2 Degree=2 IsPeriodic=0
    g11: BSplineCurve PolesCount=2 KnotsCount=2 Degree=1 IsPeriodic=0
    g12: BSplineCurve PolesCount=3 KnotsCount=2 Degree=2 IsPeriodic=0
    g13: BSplineCurve PolesCount=3 KnotsCount=2 Degree=2 IsPeriodic=0
    g14: BSplineCurve PolesCount=2 KnotsCount=2 Degree=1 IsPeriodic=0
    g15: BSplineCurve PolesCount=2 KnotsCount=2 Degree=1 IsPeriodic=0
    g16: BSplineCurve PolesCount=2 KnotsCount=2 Degree=1 IsPeriodic=0
    g17: BSplineCurve PolesCount=2 KnotsCount=2 Degree=1 IsPeriodic=0
    g18: BSplineCurve PolesCount=2 KnotsCount=2 Degree=1 IsPeriodic=0
    g19: BSplineCurve PolesCount=2 KnotsCount=2 Degree=1 IsPeriodic=0
    g20: BSplineCurve PolesCount=3 KnotsCount=2 Degree=2 IsPeriodic=0
    g21: BSplineCurve PolesCount=2 KnotsCount=2 Degree=1 IsPeriodic=0
    g22: BSplineCurve PolesCount=3 KnotsCount=2 Degree=2 IsPeriodic=0
    g23: BSplineCurve PolesCount=3 KnotsCount=2 Degree=2 IsPeriodic=0
    g24: BSplineCurve PolesCount=2 KnotsCount=2 Degree=1 IsPeriodic=0
    g25: BSplineCurve PolesCount=3 KnotsCount=2 Degree=2 IsPeriodic=0
    g26: BSplineCurve PolesCount=3 KnotsCount=2 Degree=2 IsPeriodic=0
    g27: BSplineCurve PolesCount=2 KnotsCount=2 Degree=1 IsPeriodic=0
    g28: BSplineCurve PolesCount=2 KnotsCount=2 Degree=1 IsPeriodic=0
    g29: BSplineCurve PolesCount=2 KnotsCount=2 Degree=1 IsPeriodic=0
    g30: BSplineCurve PolesCount=2 KnotsCount=2 Degree=1 IsPeriodic=0
    g31: BSplineCurve PolesCount=2 KnotsCount=2 Degree=1 IsPeriodic=0
    g32: BSplineCurve PolesCount=2 KnotsCount=2 Degree=1 IsPeriodic=0
    g33: BSplineCurve PolesCount=3 KnotsCount=2 Degree=2 IsPeriodic=0
    g34: BSplineCurve PolesCount=2 KnotsCount=2 Degree=1 IsPeriodic=0
    g35: LineSegment StartX=78.0131 StartY=-169.665 StartZ=0 EndX=78.8 EndY=-169.67 EndZ=0
    g36: LineSegment StartX=69.36 StartY=-167.41 StartZ=0 EndX=70.06 EndY=-167.76 EndZ=0
    g37: LineSegment StartX=68.79 StartY=-169.79 StartZ=0 EndX=69.0243 EndY=-168.821 EndZ=0
    g38: LineSegment StartX=69.1383 StartY=-168.357 StartZ=0 EndX=69.36 EndY=-167.41 EndZ=0
    g39: LineSegment StartX=68.4883 StartY=-168.702 StartZ=0 EndX=69.0243 EndY=-168.821 EndZ=0
    g40: LineSegment StartX=68.6008 StartY=-168.232 StartZ=0 EndX=69.1383 EndY=-168.357 EndZ=0
  constraints (53):
    c: Coincident(g0,g1)
    c: Coincident(g1,g2)
    c: Coincident(g2,g3)
    c: Coincident(g3,g4)
    c: Coincident(g4,g5)
    c: Coincident(g5,g6)
    c: Coincident(g6,g7)
    c: Coincident(g7,g8)
    c: Coincident(g8,g0)
    c: Coincident(g9,g10)
    c: Coincident(g10,g11)
    c: Coincident(g11,g12)
    c: Coincident(g12,g13)
    c: Coincident(g13,g14)
    c: Coincident(g14,g15)
    c: Coincident(g15,g16)
    c: Coincident(g16,g17)
    c: Coincident(g17,g18)
    c: Coincident(g18,g19)
    c: Coincident(g19,g20)
    c: Coincident(g20,g21)
    c: Coincident(g21,g22)
    c: Coincident(g22,g23)
    c: Coincident(g23,g24)
    c: Coincident(g24,g25)
    c: Coincident(g25,g26)
    c: Coincident(g26,g27)
    c: Coincident(g27,g28)
    c: Coincident(g28,g29)
    c: Coincident(g29,g30)
    c: Coincident(g30,g31)
    c: Coincident(g31,g32)
    c: Coincident(g32,g33)
    c: Coincident(g33,g34)
    c: Coincident(g34,g9)
    c: Coincident(g35,g17)
    c: DistanceX(g10) = 78.8
    c: DistanceY(g10) = -169.67
    c: Coincident(g35,g10)
    c: DistanceX(g24) = 69.36
    c: DistanceY(g24) = -167.41
    c: DistanceX(g30) = 70.06
    c: DistanceY(g30) = -167.76
    c: Coincident(g36,g24)
    c: Coincident(g36,g30)
    c: DistanceX(g23) = 68.79
    c: DistanceY(g23) = -169.79
    c: Coincident(g37,g23)
    c: Coincident(g38,g36)
    c: Coincident(g39,g1)
    c: Coincident(g39,g37)
    c: Coincident(g40,g0)
    c: Coincident(g40,g38)
FEATURE [Sketcher::SketchObject] Sketch005  label="EScaffoldSketch"
  FullyConstrained = false
  Placement = pos=(-105.3,177.4,0) rot=(0,0,1;0rad)
  expr: .Placement.Base.x = Spreadsheet.dim_text_x
  expr: .Placement.Base.y = Spreadsheet.dim_text_y
  sketch-geometry (30):
    g0: BSplineCurve PolesCount=3 KnotsCount=2 Degree=2 IsPeriodic=0
    g1: BSplineCurve PolesCount=2 KnotsCount=2 Degree=1 IsPeriodic=0
    g2: BSplineCurve PolesCount=3 KnotsCount=2 Degree=2 IsPeriodic=0
    g3: BSplineCurve PolesCount=2 KnotsCount=2 Degree=1 IsPeriodic=0
    g4: BSplineCurve PolesCount=3 KnotsCount=2 Degree=2 IsPeriodic=0
    g5: BSplineCurve PolesCount=2 KnotsCount=2 Degree=1 IsPeriodic=0
    g6: BSplineCurve PolesCount=3 KnotsCount=2 Degree=2 IsPeriodic=0
    g7: BSplineCurve PolesCount=2 KnotsCount=2 Degree=1 IsPeriodic=0
    g8: BSplineCurve PolesCount=2 KnotsCount=2 Degree=1 IsPeriodic=0
    g9: BSplineCurve PolesCount=2 KnotsCount=2 Degree=1 IsPeriodic=0
    g10: BSplineCurve PolesCount=2 KnotsCount=2 Degree=1 IsPeriodic=0
    g11: BSplineCurve PolesCount=2 KnotsCount=2 Degree=1 IsPeriodic=0
    g12: BSplineCurve PolesCount=2 KnotsCount=2 Degree=1 IsPeriodic=0
    g13: BSplineCurve PolesCount=2 KnotsCount=2 Degree=1 IsPeriodic=0
    g14: BSplineCurve PolesCount=2 KnotsCount=2 Degree=1 IsPeriodic=0
    g15: BSplineCurve PolesCount=2 KnotsCount=2 Degree=1 IsPeriodic=0
    g16: BSplineCurve PolesCount=2 KnotsCount=2 Degree=1 IsPeriodic=0
    g17: BSplineCurve PolesCount=2 KnotsCount=2 Degree=1 IsPeriodic=0
    g18: BSplineCurve PolesCount=2 KnotsCount=2 Degree=1 IsPeriodic=0
    g19: BSplineCurve PolesCount=2 KnotsCount=2 Degree=1 IsPeriodic=0
    g20: BSplineCurve PolesCount=2 KnotsCount=2 Degree=1 IsPeriodic=0
    g21: BSplineCurve PolesCount=2 KnotsCount=2 Degree=1 IsPeriodic=0
    g22: BSplineCurve PolesCount=2 KnotsCount=2 Degree=1 IsPeriodic=0
    g23: BSplineCurve PolesCount=2 KnotsCount=2 Degree=1 IsPeriodic=0
    g24: BSplineCurve PolesCount=2 KnotsCount=2 Degree=1 IsPeriodic=0
    g25: LineSegment StartX=94.75 StartY=-151.84 StartZ=0 EndX=94.61 EndY=-151.15 EndZ=0
    g26: LineSegment StartX=92.65 StartY=-146.18 StartZ=0 EndX=92.817 EndY=-146.12 EndZ=0
    g27: LineSegment StartX=94.51 StartY=-145.49 StartZ=0 EndX=93.3792 EndY=-145.911 EndZ=0
    g28: LineSegment StartX=93.3792 StartY=-145.911 StartZ=0 EndX=93.2 EndY=-145.41 EndZ=0
    g29: LineSegment StartX=92.817 StartY=-146.12 StartZ=0 EndX=92.66 EndY=-145.61 EndZ=0
  constraints (45):
    c: Coincident(g0,g1)
    c: Coincident(g1,g2)
    c: Coincident(g2,g3)
    c: Coincident(g3,g4)
    c: Coincident(g4,g5)
    c: Coincident(g5,g6)
    c: Coincident(g6,g7)
    c: Coincident(g7,g8)
    c: Coincident(g8,g9)
    c: Coincident(g9,g10)
    c: Coincident(g10,g11)
    c: Coincident(g11,g12)
    c: Coincident(g12,g13)
    c: Coincident(g13,g14)
    c: Coincident(g14,g0)
    c: Coincident(g15,g16)
    c: Coincident(g16,g17)
    c: Coincident(g17,g18)
    c: Coincident(g18,g15)
    c: Coincident(g19,g20)
    c: Coincident(g20,g21)
    c: Coincident(g21,g22)
    c: Coincident(g22,g23)
    c: Coincident(g23,g24)
    c: Coincident(g24,g19)
    c: DistanceX(g10) = 94.61
    c: DistanceY(g10) = -151.15
    c: DistanceX(g2) = 94.75
    c: DistanceY(g2) = -151.84
    c: Coincident(g25,g2)
    c: Coincident(g25,g10)
    c: DistanceX(g4) = 92.65
    c: DistanceY(g4) = -146.18
    c: DistanceX(g5) = 94.51
    c: DistanceY(g5) = -145.49
    c: DistanceX(g19) = 93.2
    c: DistanceY(g19) = -145.41
    c: DistanceX(g20) = 92.66
    c: DistanceY(g20) = -145.61
    c: Coincident(g26,g4)
    c: Coincident(g27,g6)
    c: Coincident(g28,g27)
    c: Coincident(g28,g19)
    c: Coincident(g29,g26)
    c: Coincident(g29,g21)
FEATURE [PartDesign::Pad] Pad001  label="TScaffoldPad"
  BaseFeature = -> Pad
  Direction = (0,0,1)
  Length = 1
  Length2 = 10
  Profile = -> Sketch003
  ReferenceAxis = -> Sketch003 [N_Axis]
  Type = 0
  expr: Length = Spreadsheet.dim_scaffold_h
FEATURE [PartDesign::Pad] Pad002  label="SScaffoldPad"
  BaseFeature = -> Pad001
  Direction = (0,0,1)
  Length = 1
  Length2 = 10
  Profile = -> Sketch004
  ReferenceAxis = -> Sketch004 [N_Axis]
  Type = 0
  expr: Length = Spreadsheet.dim_scaffold_h
FEATURE [PartDesign::Pad] Pad003  label="EScaffoldPad"
  BaseFeature = -> Pad002
  Direction = (0,0,1)
  Length = 1
  Length2 = 10
  Profile = -> Sketch005
  ReferenceAxis = -> Sketch005 [N_Axis]
  Type = 0
  expr: Length = Spreadsheet.dim_scaffold_h
FEATURE [PartDesign::Pad] Pad004  label="NarozeninyPad"
  BaseFeature = -> Pad003
  Direction = (0,0,1)
  Length = 2
  Length2 = 10
  Profile = -> Sketch002
  ReferenceAxis = -> Sketch002 [N_Axis]
  Type = 0
  expr: Length = Spreadsheet.dim_text_h
FEATURE [Sketcher::SketchObject] Sketch006  label="SSketch"
  FullyConstrained = false
  Placement = pos=(-105.3,177.4,0) rot=(0,0,1;0rad)
  expr: .Placement.Base.x = Spreadsheet.dim_text_x
  expr: .Placement.Base.y = Spreadsheet.dim_text_y
  sketch-geometry (9):
    g0: BSplineCurve PolesCount=2 KnotsCount=2 Degree=1 IsPeriodic=0
    g1: BSplineCurve PolesCount=2 KnotsCount=2 Degree=1 IsPeriodic=0
    g2: BSplineCurve PolesCount=2 KnotsCount=2 Degree=1 IsPeriodic=0
    g3: BSplineCurve PolesCount=2 KnotsCount=2 Degree=1 IsPeriodic=0
    g4: BSplineCurve PolesCount=2 KnotsCount=2 Degree=1 IsPeriodic=0
    g5: BSplineCurve PolesCount=2 KnotsCount=2 Degree=1 IsPeriodic=0
    g6: BSplineCurve PolesCount=2 KnotsCount=2 Degree=1 IsPeriodic=0
    g7: BSplineCurve PolesCount=2 KnotsCount=2 Degree=1 IsPeriodic=0
    g8: BSplineCurve PolesCount=2 KnotsCount=2 Degree=1 IsPeriodic=0
  constraints (9):
    c: Coincident(g0,g1)
    c: Coincident(g1,g2)
    c: Coincident(g2,g3)
    c: Coincident(g3,g4)
    c: Coincident(g4,g5)
    c: Coincident(g5,g6)
    c: Coincident(g6,g7)
    c: Coincident(g7,g8)
    c: Coincident(g8,g0)
FEATURE [PartDesign::Pad] Pad005  label="astnePad"
  BaseFeature = -> Pad004
  Direction = (0,0,1)
  Length = 2
  Length2 = 10
  Profile = -> Sketch
  ReferenceAxis = -> Sketch [N_Axis]
  Type = 0
  expr: Length = Spreadsheet.dim_text_h
FEATURE [PartDesign::Pad] Pad006  label="SAccentPad"
  BaseFeature = -> Pad005
  Direction = (0,0,1)
  Length = 2
  Length2 = 10
  Profile = -> Sketch006
  ReferenceAxis = -> Sketch006 [N_Axis]
  Type = 0
  expr: Length = Spreadsheet.dim_text_h
FEATURE [Sketcher::SketchObject] Sketch007  label="TSketch"
  FullyConstrained = false
  Placement = pos=(-105.3,177.4,0) rot=(0,0,1;0rad)
  expr: .Placement.Base.x = Spreadsheet.dim_text_x
  expr: .Placement.Base.y = Spreadsheet.dim_text_y
  sketch-geometry (21):
    g0: BSplineCurve PolesCount=3 KnotsCount=2 Degree=2 IsPeriodic=0
    g1: BSplineCurve PolesCount=3 KnotsCount=2 Degree=2 IsPeriodic=0
    g2: BSplineCurve PolesCount=2 KnotsCount=2 Degree=1 IsPeriodic=0
    g3: BSplineCurve PolesCount=3 KnotsCount=2 Degree=2 IsPeriodic=0
    g4: BSplineCurve PolesCount=3 KnotsCount=2 Degree=2 IsPeriodic=0
    g5: BSplineCurve PolesCount=3 KnotsCount=2 Degree=2 IsPeriodic=0
    g6: BSplineCurve PolesCount=3 KnotsCount=2 Degree=2 IsPeriodic=0
    g7: BSplineCurve PolesCount=3 KnotsCount=2 Degree=2 IsPeriodic=0
    g8: BSplineCurve PolesCount=2 KnotsCount=2 Degree=1 IsPeriodic=0
    g9: BSplineCurve PolesCount=2 KnotsCount=2 Degree=1 IsPeriodic=0
    g10: BSplineCurve PolesCount=2 KnotsCount=2 Degree=1 IsPeriodic=0
    g11: BSplineCurve PolesCount=2 KnotsCount=2 Degree=1 IsPeriodic=0
    g12: BSplineCurve PolesCount=2 KnotsCount=2 Degree=1 IsPeriodic=0
    g13: BSplineCurve PolesCount=2 KnotsCount=2 Degree=1 IsPeriodic=0
    g14: BSplineCurve PolesCount=2 KnotsCount=2 Degree=1 IsPeriodic=0
    g15: BSplineCurve PolesCount=2 KnotsCount=2 Degree=1 IsPeriodic=0
    g16: BSplineCurve PolesCount=2 KnotsCount=2 Degree=1 IsPeriodic=0
    g17: BSplineCurve PolesCount=2 KnotsCount=2 Degree=1 IsPeriodic=0
    g18: BSplineCurve PolesCount=2 KnotsCount=2 Degree=1 IsPeriodic=0
    g19: BSplineCurve PolesCount=3 KnotsCount=2 Degree=2 IsPeriodic=0
    g20: BSplineCurve PolesCount=3 KnotsCount=2 Degree=2 IsPeriodic=0
  constraints (29):
    c: Coincident(g0,g1)
    c: Coincident(g1,g2)
    c: Coincident(g2,g3)
    c: Coincident(g3,g4)
    c: Coincident(g4,g5)
    c: Coincident(g5,g6)
    c: Coincident(g6,g7)
    c: Coincident(g7,g8)
    c: Coincident(g8,g9)
    c: Coincident(g9,g10)
    c: Coincident(g10,g11)
    c: Coincident(g11,g12)
    c: Coincident(g12,g13)
    c: Coincident(g13,g14)
    c: Coincident(g14,g15)
    c: Coincident(g15,g16)
    c: Coincident(g16,g17)
    c: Coincident(g17,g18)
    c: Coincident(g18,g19)
    c: Coincident(g19,g20)
    c: Coincident(g20,g0)
    c: DistanceX(g0) = 79.97
    c: DistanceY(g0) = -164.39
    c: DistanceX(g3) = 80.75
    c: DistanceY(g3) = -164.82
    c: DistanceX(g2) = 80.83
    c: DistanceY(g2) = -164.3
    c: DistanceX(g1) = 80.05
    c: DistanceY(g1) = -163.96
FEATURE [PartDesign::Pad] Pad007  label="TPad"
  BaseFeature = -> Pad006
  Direction = (0,0,1)
  Length = 2
  Length2 = 10
  Profile = -> Sketch007
  ReferenceAxis = -> Sketch007 [N_Axis]
  Type = 0
  expr: Length = Spreadsheet.dim_text_h
FEATURE [Sketcher::SketchObject] Sketch008  label="TAccentSketch"
  FullyConstrained = false
  Placement = pos=(-105.3,177.4,0) rot=(0,0,1;0rad)
  expr: .Placement.Base.x = Spreadsheet.dim_text_x
  expr: .Placement.Base.y = Spreadsheet.dim_text_y
  sketch-geometry (10):
    g0: BSplineCurve PolesCount=2 KnotsCount=2 Degree=1 IsPeriodic=0
    g1: BSplineCurve PolesCount=3 KnotsCount=2 Degree=2 IsPeriodic=0
    g2: BSplineCurve PolesCount=3 KnotsCount=2 Degree=2 IsPeriodic=0
    g3: BSplineCurve PolesCount=3 KnotsCount=2 Degree=2 IsPeriodic=0
    g4: BSplineCurve PolesCount=2 KnotsCount=2 Degree=1 IsPeriodic=0
    g5: BSplineCurve PolesCount=2 KnotsCount=2 Degree=1 IsPeriodic=0
    g6: BSplineCurve PolesCount=3 KnotsCount=2 Degree=2 IsPeriodic=0
    g7: BSplineCurve PolesCount=3 KnotsCount=2 Degree=2 IsPeriodic=0
    g8: BSplineCurve PolesCount=3 KnotsCount=2 Degree=2 IsPeriodic=0
    g9: BSplineCurve PolesCount=2 KnotsCount=2 Degree=1 IsPeriodic=0
  constraints (10):
    c: Coincident(g0,g1)
    c: Coincident(g1,g2)
    c: Coincident(g2,g3)
    c: Coincident(g3,g4)
    c: Coincident(g4,g5)
    c: Coincident(g5,g6)
    c: Coincident(g6,g7)
    c: Coincident(g7,g8)
    c: Coincident(g8,g9)
    c: Coincident(g9,g0)
FEATURE [PartDesign::Pad] Pad008  label="TAccentPad"
  BaseFeature = -> Pad007
  Direction = (0,0,1)
  Length = 2
  Length2 = 10
  Profile = -> Sketch008
  ReferenceAxis = -> Sketch008 [N_Axis]
  Type = 0
  expr: Length = Spreadsheet.dim_text_h
FEATURE [Sketcher::SketchObject] Sketch009  label="SSketch001"
  FullyConstrained = false
  Placement = pos=(-105.3,177.4,0) rot=(0,0,1;0rad)
  expr: .Placement.Base.x = Spreadsheet.dim_text_x
  expr: .Placement.Base.y = Spreadsheet.dim_text_y
  sketch-geometry (26):
    g0: BSplineCurve PolesCount=3 KnotsCount=2 Degree=2 IsPeriodic=0
    g1: BSplineCurve PolesCount=3 KnotsCount=2 Degree=2 IsPeriodic=0
    g2: BSplineCurve PolesCount=2 KnotsCount=2 Degree=1 IsPeriodic=0
    g3: BSplineCurve PolesCount=3 KnotsCount=2 Degree=2 IsPeriodic=0
    g4: BSplineCurve PolesCount=3 KnotsCount=2 Degree=2 IsPeriodic=0
    g5: BSplineCurve PolesCount=2 KnotsCount=2 Degree=1 IsPeriodic=0
    g6: BSplineCurve PolesCount=2 KnotsCount=2 Degree=1 IsPeriodic=0
    g7: BSplineCurve PolesCount=2 KnotsCount=2 Degree=1 IsPeriodic=0
    g8: BSplineCurve PolesCount=2 KnotsCount=2 Degree=1 IsPeriodic=0
    g9: BSplineCurve PolesCount=2 KnotsCount=2 Degree=1 IsPeriodic=0
    g10: BSplineCurve PolesCount=2 KnotsCount=2 Degree=1 IsPeriodic=0
    g11: BSplineCurve PolesCount=3 KnotsCount=2 Degree=2 IsPeriodic=0
    g12: BSplineCurve PolesCount=2 KnotsCount=2 Degree=1 IsPeriodic=0
    g13: BSplineCurve PolesCount=3 KnotsCount=2 Degree=2 IsPeriodic=0
    g14: BSplineCurve PolesCount=3 KnotsCount=2 Degree=2 IsPeriodic=0
    g15: BSplineCurve PolesCount=2 KnotsCount=2 Degree=1 IsPeriodic=0
    g16: BSplineCurve PolesCount=3 KnotsCount=2 Degree=2 IsPeriodic=0
    g17: BSplineCurve PolesCount=3 KnotsCount=2 Degree=2 IsPeriodic=0
    g18: BSplineCurve PolesCount=2 KnotsCount=2 Degree=1 IsPeriodic=0
    g19: BSplineCurve PolesCount=2 KnotsCount=2 Degree=1 IsPeriodic=0
    g20: BSplineCurve PolesCount=2 KnotsCount=2 Degree=1 IsPeriodic=0
    g21: BSplineCurve PolesCount=2 KnotsCount=2 Degree=1 IsPeriodic=0
    g22: BSplineCurve PolesCount=2 KnotsCount=2 Degree=1 IsPeriodic=0
    g23: BSplineCurve PolesCount=2 KnotsCount=2 Degree=1 IsPeriodic=0
    g24: BSplineCurve PolesCount=3 KnotsCount=2 Degree=2 IsPeriodic=0
    g25: BSplineCurve PolesCount=2 KnotsCount=2 Degree=1 IsPeriodic=0
  constraints (26):
    c: Coincident(g0,g1)
    c: Coincident(g1,g2)
    c: Coincident(g2,g3)
    c: Coincident(g3,g4)
    c: Coincident(g4,g5)
    c: Coincident(g5,g6)
    c: Coincident(g6,g7)
    c: Coincident(g7,g8)
    c: Coincident(g8,g9)
    c: Coincident(g9,g10)
    c: Coincident(g10,g11)
    c: Coincident(g11,g12)
    c: Coincident(g12,g13)
    c: Coincident(g13,g14)
    c: Coincident(g14,g15)
    c: Coincident(g15,g16)
    c: Coincident(g16,g17)
    c: Coincident(g17,g18)
    c: Coincident(g18,g19)
    c: Coincident(g19,g20)
    c: Coincident(g20,g21)
    c: Coincident(g21,g22)
    c: Coincident(g22,g23)
    c: Coincident(g23,g24)
    c: Coincident(g24,g25)
    c: Coincident(g25,g0)
FEATURE [PartDesign::Body] Body
  Group = -> [DatumPlane,Sketch001,Pad,Sketch,Sketch002,Sketch003,Sketch004,Sketch005,Pad001,Pad002,Pad003,Pad004,Sketch006,Pad005,Pad006,Sketch007,Pad007,Sketch008,Pad008,Sketch009]
  Origin = -> Origin
  Tip = -> Pad008
FEATURE [Sketcher::SketchObject] Sketch010  label="SSketch002"
  FullyConstrained = false
  Placement = pos=(-105.3,177.4,0) rot=(0,0,1;0rad)
  expr: .Placement.Base.x = Spreadsheet.dim_text_x
  expr: .Placement.Base.y = Spreadsheet.dim_text_y
  sketch-geometry (26):
    g0: BSplineCurve PolesCount=3 KnotsCount=2 Degree=2 IsPeriodic=0
    g1: BSplineCurve PolesCount=3 KnotsCount=2 Degree=2 IsPeriodic=0
    g2: BSplineCurve PolesCount=2 KnotsCount=2 Degree=1 IsPeriodic=0
    g3: BSplineCurve PolesCount=3 KnotsCount=2 Degree=2 IsPeriodic=0
    g4: BSplineCurve PolesCount=3 KnotsCount=2 Degree=2 IsPeriodic=0
    g5: BSplineCurve PolesCount=2 KnotsCount=2 Degree=1 IsPeriodic=0
    g6: BSplineCurve PolesCount=2 KnotsCount=2 Degree=1 IsPeriodic=0
    g7: BSplineCurve PolesCount=2 KnotsCount=2 Degree=1 IsPeriodic=0
    g8: BSplineCurve PolesCount=2 KnotsCount=2 Degree=1 IsPeriodic=0
    g9: BSplineCurve PolesCount=2 KnotsCount=2 Degree=1 IsPeriodic=0
    g10: BSplineCurve PolesCount=2 KnotsCount=2 Degree=1 IsPeriodic=0
    g11: BSplineCurve PolesCount=3 KnotsCount=2 Degree=2 IsPeriodic=0
    g12: BSplineCurve PolesCount=2 KnotsCount=2 Degree=1 IsPeriodic=0
    g13: BSplineCurve PolesCount=3 KnotsCount=2 Degree=2 IsPeriodic=0
    g14: BSplineCurve PolesCount=3 KnotsCount=2 Degree=2 IsPeriodic=0
    g15: BSplineCurve PolesCount=2 KnotsCount=2 Degree=1 IsPeriodic=0
    g16: BSplineCurve PolesCount=3 KnotsCount=2 Degree=2 IsPeriodic=0
    g17: BSplineCurve PolesCount=3 KnotsCount=2 Degree=2 IsPeriodic=0
    g18: BSplineCurve PolesCount=2 KnotsCount=2 Degree=1 IsPeriodic=0
    g19: BSplineCurve PolesCount=2 KnotsCount=2 Degree=1 IsPeriodic=0
    g20: BSplineCurve PolesCount=2 KnotsCount=2 Degree=1 IsPeriodic=0
    g21: BSplineCurve PolesCount=2 KnotsCount=2 Degree=1 IsPeriodic=0
    g22: BSplineCurve PolesCount=2 KnotsCount=2 Degree=1 IsPeriodic=0
    g23: BSplineCurve PolesCount=2 KnotsCount=2 Degree=1 IsPeriodic=0
    g24: BSplineCurve PolesCount=3 KnotsCount=2 Degree=2 IsPeriodic=0
    g25: BSplineCurve PolesCount=2 KnotsCount=2 Degree=1 IsPeriodic=0
  constraints (26):
    c: Coincident(g0,g1)
    c: Coincident(g1,g2)
    c: Coincident(g2,g3)
    c: Coincident(g3,g4)
    c: Coincident(g4,g5)
    c: Coincident(g5,g6)
    c: Coincident(g6,g7)
    c: Coincident(g7,g8)
    c: Coincident(g8,g9)
    c: Coincident(g9,g10)
    c: Coincident(g10,g11)
    c: Coincident(g11,g12)
    c: Coincident(g12,g13)
    c: Coincident(g13,g14)
    c: Coincident(g14,g15)
    c: Coincident(g15,g16)
    c: Coincident(g16,g17)
    c: Coincident(g17,g18)
    c: Coincident(g18,g19)
    c: Coincident(g19,g20)
    c: Coincident(g20,g21)
    c: Coincident(g21,g22)
    c: Coincident(g22,g23)
    c: Coincident(g23,g24)
    c: Coincident(g24,g25)
    c: Coincident(g25,g0)
FEATURE [PartDesign::Pad] Pad009
  Direction = (0,0,1)
  Length = 2
  Length2 = 10
  Placement = pos=(-105.3,177.4,0) rot=(0,0,1;0rad)
  Profile = -> Sketch010
  ReferenceAxis = -> Sketch010 [N_Axis]
  Type = 0
  expr: Length = Spreadsheet.dim_text_h
FEATURE [PartDesign::Body] Body001
  Group = -> [Sketch010,Pad009]
  Origin = -> Origin001
  Tip = -> Pad009
FEATURE [App::Part] Part
  Group = -> [Body001,Body]
  Origin = -> Origin002
FEATURE [Mesh::Feature] Mesh  label="Part (Meshed)"
